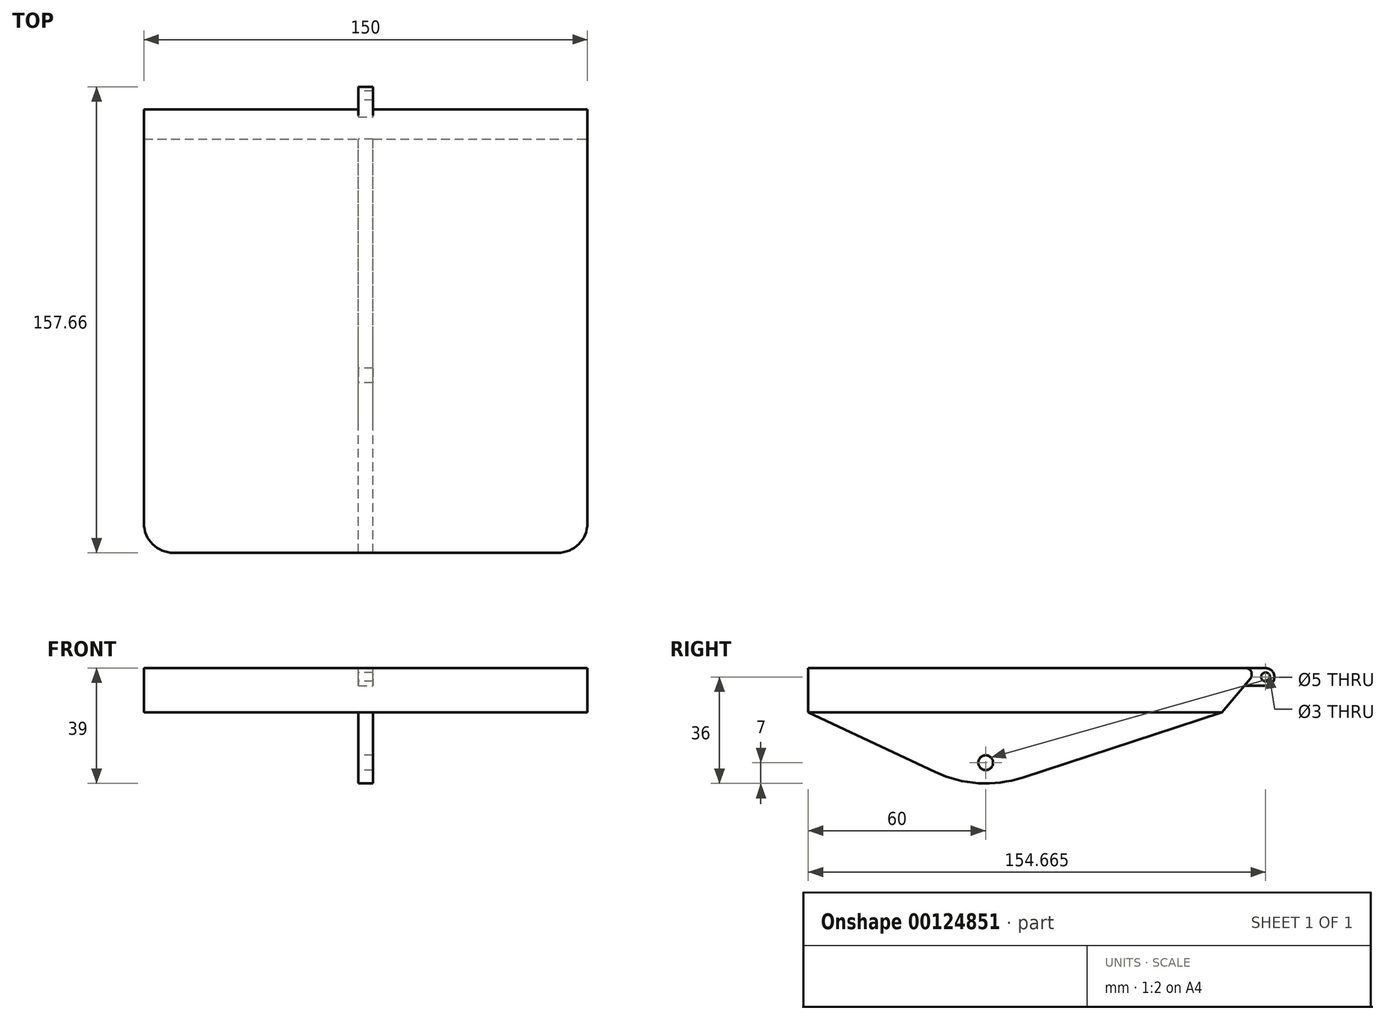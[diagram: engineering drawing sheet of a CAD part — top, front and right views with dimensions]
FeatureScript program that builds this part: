
annotation { "Feature Type Name" : "Feature", "Feature Type Description" : "" }
export const myFeature = defineFeature(function(context is Context, id is Id, definition is map)
    precondition{}
    {
        {
            var Q0;
            Q0=qCreatedBy(makeId("Right.planeOp"),FACE);
            var sketch = newSketch(context, id + "F0", { "sketchPlane" : qUnion([Q0])});
            skLineSegment(sketch, "E0.bottom", {"start": v(-60, 32) * mm, "end": v(90, 32) * mm});
            skLineSegment(sketch, "E0.top", {"start": v(-60, 17) * mm, "end": v(90, 17) * mm});
            skLineSegment(sketch, "E0.left", {"start": v(-60, 32) * mm, "end": v(-60, 17) * mm});
            skLineSegment(sketch, "E0.right", {"start": v(90, 32) * mm, "end": v(90, 17) * mm});
            skSolve(sketch);
        }
        {
            var Q0;
            Q0 = qSketchRegion(id + "F0", true);
            extrude(context, id + "F1", {"entities" : qUnion([Q0]), "endBound" : BoundingType.SYMMETRIC, "depth" : 150 * mm});
        }
        {
            var Q0;
            Q0=makeQuery(id+"F1.opExtrude","SWEPT_EDGE",EDGE,{"disambiguationData":[OSD([sQuery(id+"F0.wireOp",EDGE,"E0.top"),sQuery(id+"F0.wireOp",EDGE,"E0.right")])]});
            chamfer(context, id + "F2", {"entities" : qUnion([Q0]), "chamferType" : ChamferType.OFFSET_ANGLE, "width" : 12 * mm, "oppositeDirection" : false, "angle" : 40 * degree, "tangentPropagation" : true});
        }
        {
            var Q0;
            Q0=makeQuery(id+"F1.opExtrude","SWEPT_EDGE",EDGE,{"disambiguationData":[OSD([sQuery(id+"F0.wireOp",EDGE,"E0.bottom"),sQuery(id+"F0.wireOp",EDGE,"E0.right")])]});
            var Q1;
            {var subQ0=sQuery(id+"F0.wireOp",EDGE,"E0.right");Q1=makeQuery(id+"F2.opChamfer","BLEND_EDGE",EDGE,{"blendedFrom":[makeQuery(id+"F1.opExtrude","SWEPT_EDGE",EDGE,{"disambiguationData":[OSD([sQuery(id+"F0.wireOp",EDGE,"E0.top"),subQ0])]}),makeQuery(id+"F1.opExtrude","SWEPT_FACE",FACE,{"disambiguationData":[OSD([subQ0])]})],"blendedInto":[makeQuery(id+"F1.opExtrude","SWEPT_FACE",FACE,{"disambiguationData":[OSD([subQ0])]})]});}
            fillet(context, id + "F3", {"entities" : qUnion([Q0, Q1]), "radius" : 2 * mm, "tangentPropagation" : true, "allowEdgeOverflow" : false});
        }
        {
            var Q0;
            Q0=qCreatedBy(makeId("Right.planeOp"),FACE);
            var sketch = newSketch(context, id + "F4", { "sketchPlane" : qUnion([Q0])});
            skLineSegment(sketch, "E1.0", {"start": v(-60, 17) * mm, "end": v(79.93, 17) * mm});
            skLineSegment(sketch, "E2", {"start": v(-60, 17) * mm, "end": v(-17.01, -3.2) * mm});
            skLineSegment(sketch, "E3", {"start": v(12.4, -5.03) * mm, "end": v(79.93, 17) * mm});
            skArc(sketch, "E4", {"start": v(-17.01, -3.2) * mm, "mid": v(-2.48, -6.92) * mm, "end": v(12.4, -5.03) * mm});
            skCircle(sketch, "E5", {"center": v(0, 0) * mm, "radius": 2.5 * mm});
            skSolve(sketch);
        }
        {
            var Q0;
            Q0 = qSketchRegion(id + "F4", true);
            extrude(context, id + "F5", {"entities" : qUnion([Q0]), "operationType" : NewBodyOperationType.ADD, "endBound" : BoundingType.SYMMETRIC, "depth" : 5 * mm});
        }
        {
            var Q0;
            Q0=qCreatedBy(makeId("Right.planeOp"),FACE);
            var sketch = newSketch(context, id + "F6", { "sketchPlane" : qUnion([Q0])});
            skLineSegment(sketch, "E6.bottom", {"start": v(84.09, 32) * mm, "end": v(94.66, 32) * mm});
            skLineSegment(sketch, "E6.top", {"start": v(84.09, 26) * mm, "end": v(94.66, 26) * mm});
            skLineSegment(sketch, "E6.left", {"start": v(84.09, 32) * mm, "end": v(84.09, 26) * mm});
            skArc(sketch, "E7", {"start": v(94.66, 26) * mm, "mid": v(97.66, 29) * mm, "end": v(94.66, 32) * mm});
            skCircle(sketch, "E8", {"center": v(94.66, 29) * mm, "radius": 1.5 * mm});
            skSolve(sketch);
        }
        {
            var Q0;
            Q0 = qSketchRegion(id + "F6", true);
            extrude(context, id + "F7", {"entities" : qUnion([Q0]), "operationType" : NewBodyOperationType.ADD, "endBound" : BoundingType.SYMMETRIC, "depth" : 5 * mm});
        }
        {
            var Q0;
            Q0=makeQuery(id+"F1.opExtrude","CAP_EDGE",EDGE,{"disambiguationData":[OSD([sQuery(id+"F0.wireOp",EDGE,"E0.left")])],"isStart":false});
            var Q1;
            Q1=makeQuery(id+"F1.opExtrude","CAP_EDGE",EDGE,{"disambiguationData":[OSD([sQuery(id+"F0.wireOp",EDGE,"E0.left")])],"isStart":true});
            fillet(context, id + "F8", {"entities" : qUnion([Q0, Q1]), "radius" : 10 * mm, "tangentPropagation" : true, "allowEdgeOverflow" : false});
        }
    });
